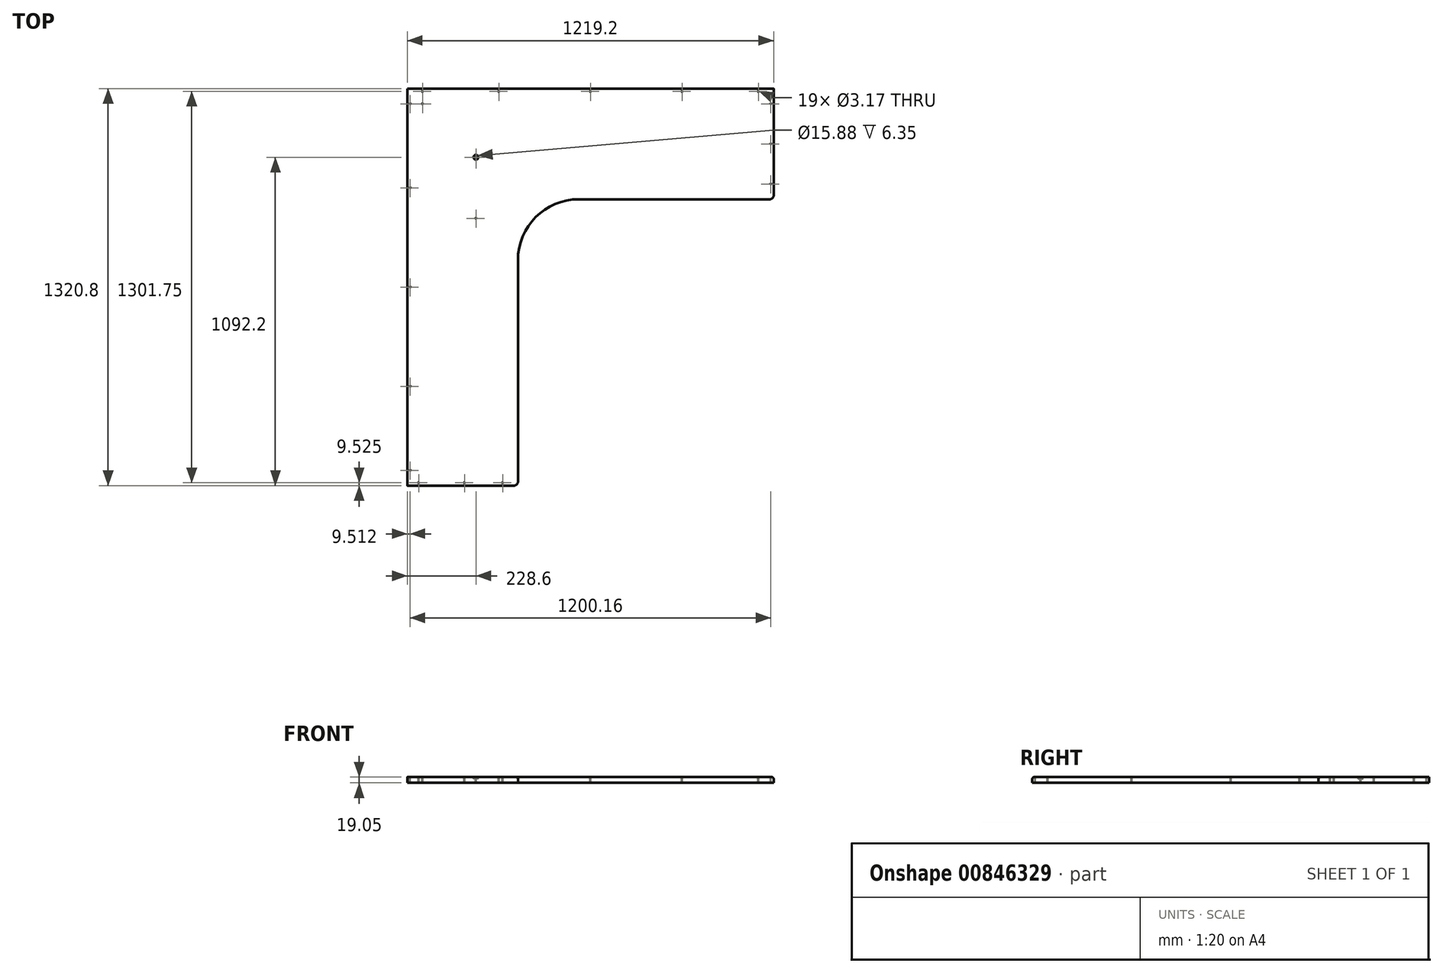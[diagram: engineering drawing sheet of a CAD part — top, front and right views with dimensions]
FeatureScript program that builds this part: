
annotation { "Feature Type Name" : "Feature", "Feature Type Description" : "" }
export const myFeature = defineFeature(function(context is Context, id is Id, definition is map)
    precondition{}
    {
        {
            var Q0;
            Q0=qCreatedBy(makeId("Top.planeOp"),FACE);
            var sketch = newSketch(context, id + "F0", { "sketchPlane" : qUnion([Q0])});
            skLineSegment(sketch, "E0.bottom", {"start": v(-571.5, -749.3) * mm, "end": v(-215.9, -749.3) * mm});
            skLineSegment(sketch, "E0.left", {"start": v(-571.5, -749.3) * mm, "end": v(-571.5, 571.5) * mm});
            skLineSegment(sketch, "E0.right", {"start": v(-203.2, -736.6) * mm, "end": v(-203.2, 0) * mm});
            skLineSegment(sketch, "E1.bottom", {"start": v(-571.5, 571.5) * mm, "end": v(647.7, 571.5) * mm});
            skLineSegment(sketch, "E1.top", {"start": v(0, 203.2) * mm, "end": v(635, 203.2) * mm});
            skArc(sketch, "E2.filletArc", {"start": v(0, 203.2) * mm, "mid": v(-143.68, 143.68) * mm, "end": v(-203.2, 0) * mm});
            skLineSegment(sketch, "E3", {"start": v(647.7, 215.9) * mm, "end": v(647.7, 571.5) * mm});
            skArc(sketch, "E4.filletArc", {"start": v(635, 203.2) * mm, "mid": v(643.98, 206.92) * mm, "end": v(647.7, 215.9) * mm});
            skCircle(sketch, "E5", {"center": v(-254, -739.78) * mm, "radius": 1.59 * mm});
            skCircle(sketch, "E6", {"center": v(-381, -739.78) * mm, "radius": 1.59 * mm});
            skCircle(sketch, "E7", {"center": v(-533.4, -739.78) * mm, "radius": 1.59 * mm});
            skCircle(sketch, "E8", {"center": v(-561.98, -698.5) * mm, "radius": 1.59 * mm});
            skCircle(sketch, "E9", {"center": v(-561.98, -419.1) * mm, "radius": 1.59 * mm});
            skCircle(sketch, "E10", {"center": v(-561.99, -88.9) * mm, "radius": 1.59 * mm});
            skCircle(sketch, "E11", {"center": v(-561.98, 520.7) * mm, "radius": 1.59 * mm});
            skCircle(sketch, "E12", {"center": v(-520.7, 561.98) * mm, "radius": 1.59 * mm});
            skCircle(sketch, "E13", {"center": v(-266.7, 561.98) * mm, "radius": 1.59 * mm});
            skCircle(sketch, "E14", {"center": v(342.9, 561.98) * mm, "radius": 1.59 * mm});
            skCircle(sketch, "E15", {"center": v(596.9, 561.98) * mm, "radius": 1.59 * mm});
            skCircle(sketch, "E16", {"center": v(638.17, 387.35) * mm, "radius": 1.59 * mm});
            skCircle(sketch, "E17", {"center": v(638.18, 254) * mm, "radius": 1.59 * mm});
            skCircle(sketch, "E18", {"center": v(-520.7, 520.7) * mm, "radius": 1.59 * mm});
            skCircle(sketch, "E19", {"center": v(-342.9, 342.9) * mm, "radius": 1.59 * mm});
            skCircle(sketch, "E20", {"center": v(-342.9, 139.7) * mm, "radius": 1.59 * mm});
            skCircle(sketch, "E21", {"center": v(-561.98, 241.3) * mm, "radius": 1.59 * mm});
            skCircle(sketch, "E22", {"center": v(38.1, 561.98) * mm, "radius": 1.59 * mm});
            skCircle(sketch, "E23", {"center": v(638.17, 520.7) * mm, "radius": 1.59 * mm});
            skArc(sketch, "E24.filletArc", {"start": v(-215.9, -749.3) * mm, "mid": v(-206.92, -745.58) * mm, "end": v(-203.2, -736.6) * mm});
            skSolve(sketch);
        }
        {
            var Q0;
            Q0=makeQuery(id+"F0.imprint","IMPRINT",FACE,{"disambiguationData":[TD([[makeQuery(id+"F0.imprint","IMPRINT",EDGE,{"derivedFrom":sQuery(id+"F0.wireOp",EDGE,"E0.bottom")}),1.0]])]});
            extrude(context, id + "F1", {"entities" : qUnion([Q0]), "oppositeDirection" : true, "depth" : 19.05 * mm, "offsetDistance" : 25.4 * mm});
        }
        {
            var Q0;
            Q0=makeQuery(id+"F1.opExtrude","CAP_EDGE",EDGE,{"disambiguationData":[OSD([sQuery(id+"F0.wireOp",EDGE,"E0.bottom")])],"isStart":true});
            fillet(context, id + "F2", {"entities" : qUnion([Q0]), "radius" : 6.35 * mm, "tangentPropagation" : true, "allowEdgeOverflow" : false});
        }
        {
            var Q0;
            Q0=makeQuery(id+"F0.imprint","IMPRINT",FACE,{"disambiguationData":[TD([[makeQuery(id+"F0.imprint","IMPRINT",EDGE,{"derivedFrom":sQuery(id+"F0.wireOp",EDGE,"E0.bottom")}),1.0]])]});
            var sketch = newSketch(context, id + "F3", { "sketchPlane" : qUnion([Q0])});
            skCircle(sketch, "E25", {"center": v(-342.9, 342.9) * mm, "radius": 7.94 * mm});
            skSolve(sketch);
        }
        {
            var Q0;
            Q0 = qSketchRegion(id + "F3", true);
            extrude(context, id + "F4", {"entities" : qUnion([Q0]), "operationType" : NewBodyOperationType.REMOVE, "oppositeDirection" : true, "depth" : 6.35 * mm, "offsetDistance" : 25.4 * mm});
        }
    });
